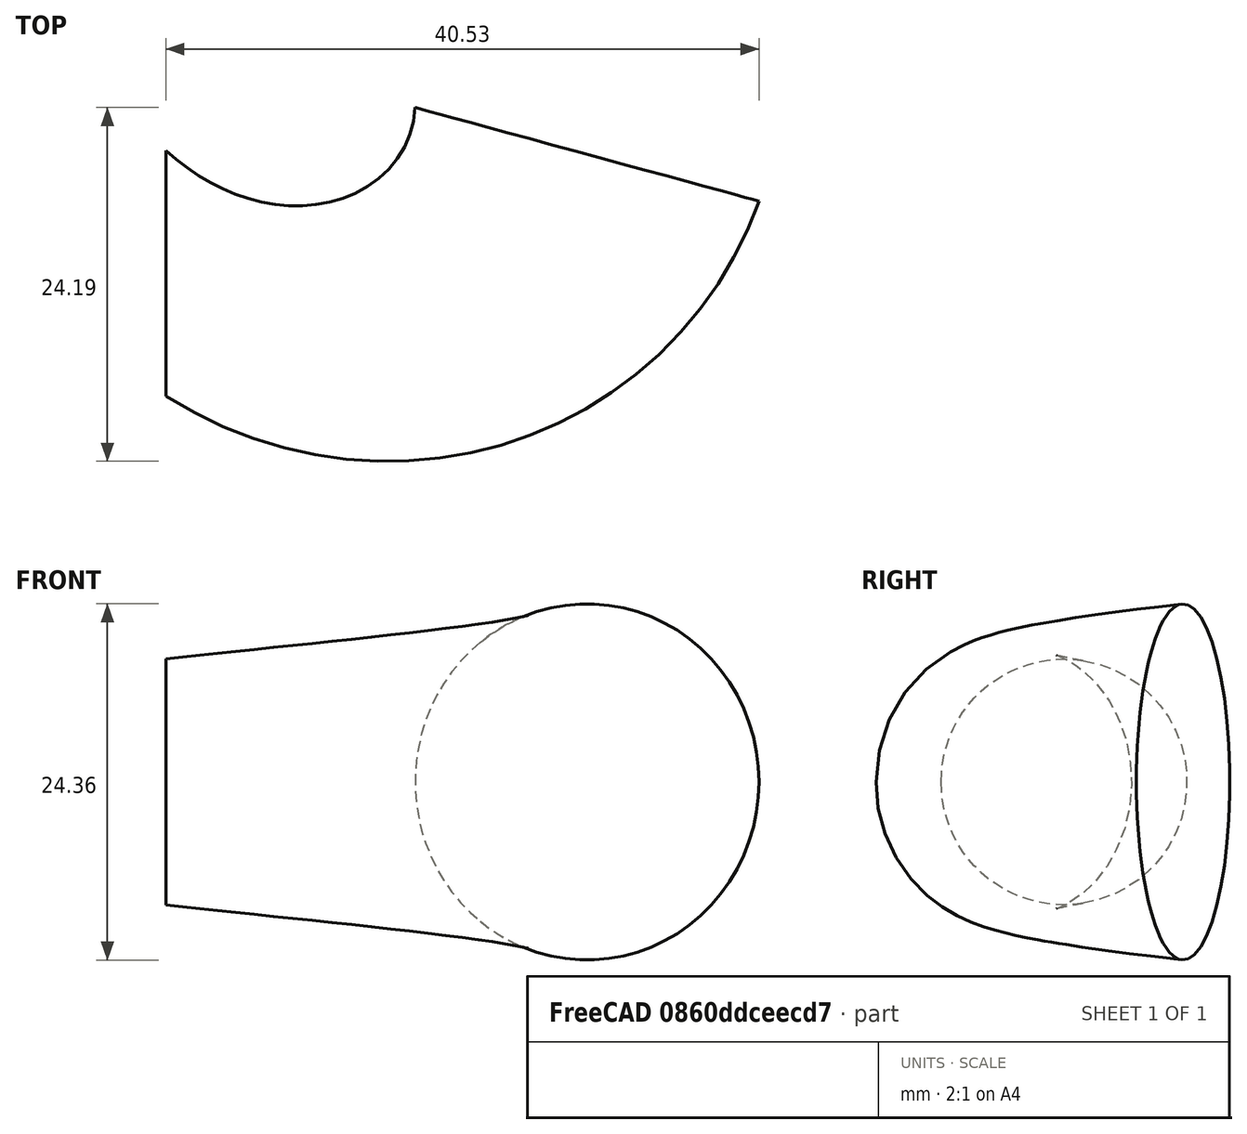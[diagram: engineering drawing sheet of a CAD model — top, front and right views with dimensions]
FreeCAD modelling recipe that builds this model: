
FCSTD DOCUMENT  (FreeCAD 1.0R39109 (Git))
Label: new-freecad
License: All rights reserved
LicenseURL: https://en.wikipedia.org/wiki/All_rights_reserved
objects: Part::Feature×25, Part::Part2DObjectPython×14, PartDesign::ShapeBinder×5, Sketcher::SketchObject×3, PartDesign::Plane×2, PartDesign::AdditivePipe×1, PartDesign::Body×1
note: 56 computed .brp shape members not serialized (recipe doc carries the construction recipe); baked Part::Feature solids carry a one-line shape summary decoded from their .brp

FEATURE [Sketcher::SketchObject] Sketch
  ArcFitTolerance = 1e-06
  AttachmentSupport = -> [XY_Plane]
  FullyConstrained = true
  MakeInternals = false
  MapMode = 5
FEATURE [Part::Feature] Line
  shape: bbox 24.24 x 2e-07 x 2e-07 mm, 0 faces, 0 solids (baked)
FEATURE [Part::Feature] Arc
  shape: bbox 16.41 x 12.57 x 2e-07 mm, 0 faces, 0 solids (baked)
FEATURE [Part::Feature] Arc001
  shape: bbox 16.41 x 12.57 x 2e-07 mm, 0 faces, 0 solids (baked)
FEATURE [Part::Feature] Line001
  shape: bbox 12.08 x 2e-07 x 2e-07 mm, 0 faces, 0 solids (baked)
FEATURE [Part::Feature] Arc002
  shape: bbox 4.831 x 3.711 x 2e-07 mm, 0 faces, 0 solids (baked)
FEATURE [Part::Feature] Arc003
  shape: bbox 4.872 x 50.24 x 2e-07 mm, 0 faces, 0 solids (baked)
FEATURE [Part::Feature] Arc004
  shape: bbox 11.42 x 106.4 x 2e-07 mm, 0 faces, 0 solids (baked)
FEATURE [Part::Feature] Line002
  shape: bbox 2e-07 x 15.35 x 2e-07 mm, 0 faces, 0 solids (baked)
FEATURE [Part::Feature] Line003
  shape: bbox 2.076 x 10.95 x 2e-07 mm, 0 faces, 0 solids (baked)
FEATURE [Part::Feature] Line004
  shape: bbox 5.231 x 2e-07 x 2e-07 mm, 0 faces, 0 solids (baked)
FEATURE [Part::Feature] Line005
  shape: bbox 13.57 x 4.192 x 2e-07 mm, 0 faces, 0 solids (baked)
FEATURE [Part::Feature] Line006
  shape: bbox 12.94 x 2.922 x 2e-07 mm, 0 faces, 0 solids (baked)
FEATURE [Part::Feature] Arc005
  shape: bbox 13.99 x 37.49 x 2e-07 mm, 0 faces, 0 solids (baked)
FEATURE [Part::Feature] Line007
  shape: bbox 3.445 x 16.84 x 2e-07 mm, 0 faces, 0 solids (baked)
FEATURE [Part::Feature] Line008
  shape: bbox 2e-07 x 0.8405 x 2e-07 mm, 0 faces, 0 solids (baked)
FEATURE [Part::Feature] Arc006
  shape: bbox 8 x 8 x 2e-07 mm, 0 faces, 0 solids (baked)
FEATURE [Part::Feature] Arc007
  shape: bbox 8 x 8 x 2e-07 mm, 0 faces, 0 solids (baked)
FEATURE [Part::Feature] Line009
  shape: bbox 2e-07 x 4.615 x 2e-07 mm, 0 faces, 0 solids (baked)
FEATURE [Part::Feature] Line010
  shape: bbox 2.883 x 9.356 x 2e-07 mm, 0 faces, 0 solids (baked)
FEATURE [Part::Feature] Arc008
  shape: bbox 0.2661 x 1.767 x 2e-07 mm, 0 faces, 0 solids (baked)
FEATURE [Part::Feature] Arc009
  shape: bbox 6.11 x 6.841 x 2e-07 mm, 0 faces, 0 solids (baked)
FEATURE [Part::Feature] Arc010
  shape: bbox 5.138 x 2.64 x 2e-07 mm, 0 faces, 0 solids (baked)
FEATURE [Part::Feature] Arc011
  shape: bbox 4 x 4 x 2e-07 mm, 0 faces, 0 solids (baked)
FEATURE [Part::Feature] Arc012
  shape: bbox 3.93 x 3.255 x 2e-07 mm, 0 faces, 0 solids (baked)
FEATURE [Part::Feature] Arc013
  shape: bbox 1.351 x 7.225 x 2e-07 mm, 0 faces, 0 solids (baked)
FEATURE [Part::Part2DObjectPython] Line012  # Draft 2D object (typed FeaturePython)
  Area = 0
  ChamferSize = 0
  Closed = false
  End = (330.971,-403.318,0)
  FilletRadius = 0
  Length = 20.7759
  MakeFace = true
  Placement = pos=(318.804,-386.478,0) rot=(0,0,1;0rad)
  Points = (2) [(0,0,0),(12.167,-16.8405,0)]
  Start = (318.804,-386.478,0)
  Subdivisions = 0
FEATURE [Part::Part2DObjectPython] Line013  # Draft 2D object (typed FeaturePython)
  Area = 0
  ChamferSize = 0
  Closed = false
  End = (347.383,-390.749,0)
  FilletRadius = 0
  Length = 25.0541
  MakeFace = true
  Placement = pos=(323.635,-382.766,0) rot=(0,0,1;0rad)
  Points = (2) [(0,0,0),(23.7484,-7.98259,0)]
  Start = (323.635,-382.766,0)
  Subdivisions = 0
FEATURE [Part::Part2DObjectPython] Line014  # Draft 2D object (typed FeaturePython)
  Area = 0
  ChamferSize = 0
  Closed = false
  End = (324.887,-394.898,0)
  FilletRadius = 0
  Length = 18.1608
  MakeFace = true
  Placement = pos=(306.727,-394.898,0) rot=(0,0,1;0rad)
  Points = (2) [(0,0,0),(18.1608,0,0)]
  Start = (306.727,-394.898,0)
  Subdivisions = 0
FEATURE [Part::Part2DObjectPython] Line015  # Draft 2D object (typed FeaturePython)
  Area = 0
  ChamferSize = 0
  Closed = false
  End = (318.782,-293.527,0)
  FilletRadius = 0
  Length = 25
  MakeFace = true
  Placement = pos=(342.094,-284.496,0) rot=(0,0,1;0rad)
  Points = (2) [(0,0,0),(-23.3117,-9.03134,0)]
  Start = (342.094,-284.496,0)
  Subdivisions = 0
FEATURE [Part::Part2DObjectPython] Line016  # Draft 2D object (typed FeaturePython)
  Area = 0
  ChamferSize = 0
  Closed = false
  End = (352.82,-330.261,0)
  FilletRadius = 0
  Length = 25
  MakeFace = true
  Placement = pos=(327.923,-332.529,0) rot=(0,0,1;0rad)
  Points = (2) [(0,0,0),(24.8969,2.26794,0)]
  Start = (327.923,-332.529,0)
  Subdivisions = 0
FEATURE [Part::Part2DObjectPython] Arc014  # Draft 2D object (typed FeaturePython)
  Area = 0
  FirstAngle = 0
  LastAngle = 36.4215
  MakeFace = false
  Placement = pos=(184.419,-345.592,0) rot=(0,0,-1;0.266003rad)
  Radius = 156.598
FEATURE [Part::Part2DObjectPython] Line017  # Draft 2D object (typed FeaturePython)
  Area = 0
  ChamferSize = 0
  Closed = false
  End = (341.307,-399.815,0)
  FilletRadius = 0
  Length = 24.1897
  MakeFace = true
  Placement = pos=(321.85,-385.443,0) rot=(0,0,1;0rad)
  Points = (2) [(0,0,0),(19.4572,-14.3721,0)]
  Start = (321.85,-385.443,0)
  Subdivisions = 0
FEATURE [Part::Part2DObjectPython] Arc015  # Draft 2D object (typed FeaturePython)
  Area = 0
  FirstAngle = 0
  LastAngle = 74.9303
  MakeFace = false
  Placement = pos=(324.887,-383.898,0) rot=(0,0,-1;1.5708rad)
  Radius = 11
FEATURE [Part::Part2DObjectPython] Line018  # Draft 2D object (typed FeaturePython)
  Area = 0
  ChamferSize = 0
  Closed = false
  End = (349.511,-309.008,0)
  FilletRadius = 0
  Length = 25
  MakeFace = true
  Placement = pos=(325.104,-314.417,0) rot=(0,0,1;0rad)
  Points = (2) [(0,0,0),(24.4079,5.40874,0)]
  Start = (325.104,-314.417,0)
  Subdivisions = 0
FEATURE [Part::Part2DObjectPython] Line019  # Draft 2D object (typed FeaturePython)
  Area = 0
  ChamferSize = 0
  Closed = false
  End = (327.923,-332.529,0)
  FilletRadius = 0
  Length = 18.3299
  MakeFace = true
  Placement = pos=(325.104,-314.417,0) rot=(0,0,1;0rad)
  Points = (2) [(0,0,0),(2.81996,-18.1117,0)]
  Start = (325.104,-314.417,0)
  Subdivisions = 0
FEATURE [Part::Part2DObjectPython] Line020  # Draft 2D object (typed FeaturePython)
  Area = 0
  ChamferSize = 0
  Closed = false
  End = (313.256,-327.03,0)
  FilletRadius = 0
  Length = 13.7263
  MakeFace = true
  Placement = pos=(326.514,-323.473,0) rot=(0,0,1;0rad)
  Points = (2) [(0,0,0),(-13.2574,-3.55713,0)]
  Start = (326.514,-323.473,0)
  Subdivisions = 0
FEATURE [Part::Part2DObjectPython] Arc016  # Draft 2D object (typed FeaturePython)
  Area = 0
  FirstAngle = 101.56
  LastAngle = 281.56
  MakeFace = true
  Placement = pos=(313.256,-327.03,0) rot=(0,0,1;0rad)
  Radius = 8.59532
FEATURE [Part::Part2DObjectPython] Line021  # Draft 2D object (typed FeaturePython)
  Area = 0
  ChamferSize = 0
  Closed = false
  End = (336.427,-266.58,0)
  FilletRadius = 0
  Length = 27.3519
  MakeFace = true
  Placement = pos=(311.109,-276.931,0) rot=(0,0,1;0rad)
  Points = (2) [(0,0,0),(25.318,10.3502,0)]
  Start = (311.109,-276.931,0)
  Subdivisions = 0
FEATURE [Part::Part2DObjectPython] Line022  # Draft 2D object (typed FeaturePython)
  Area = 0
  ChamferSize = 0
  Closed = false
  End = (330.438,-289.011,0)
  FilletRadius = 0
  Length = 18.5002
  MakeFace = true
  Placement = pos=(323.768,-271.755,0) rot=(0,0,1;0rad)
  Points = (2) [(0,0,0),(6.67012,-17.256,0)]
  Start = (323.768,-271.755,0)
  Subdivisions = 0
FEATURE [PartDesign::ShapeBinder] CopyLine014
  Placement = pos=(306.727,-394.898,0) rot=(0,0,1;0rad)
  TraceSupport = false
FEATURE [PartDesign::ShapeBinder] CopyLine015
  Placement = pos=(306.727,-394.898,0) rot=(0,0,1;0rad)
  TraceSupport = false
FEATURE [PartDesign::Plane] DatumPlane
  AttachmentSupport = -> [CopyLine014,CopyLine015]
  Length = 468.518
  MapMode = 7
  Placement = pos=(306.727,-394.898,0) rot=(0.57735,-0.57735,-0.57735;2.0944rad)
  ResizeMode = 0
  Width = 79.6274
FEATURE [Sketcher::SketchObject] Sketch001
  ArcFitTolerance = 1e-06
  AttachmentSupport = -> [DatumPlane]
  FullyConstrained = true
  MakeInternals = false
  MapMode = 5
  Placement = pos=(306.727,-394.898,0) rot=(0.57735,-0.57735,-0.57735;2.0944rad)
  sketch-geometry (1):
    g0: Circle CenterX=0 CenterY=0 CenterZ=0 NormalX=0 NormalY=0 NormalZ=1 AngleXU=0 Radius=8.4
  constraints (2):
    c: Coincident(g0,g-1)
    c: Diameter(g0) = 16.8
FEATURE [PartDesign::ShapeBinder] CopyArc014
  Placement = pos=(184.419,-345.592,0) rot=(0,0,-1;0.266003rad)
  TraceSupport = false
FEATURE [PartDesign::ShapeBinder] CopyArc015
  Placement = pos=(184.419,-345.592,0) rot=(0,0,-1;0.266003rad)
  TraceSupport = false
FEATURE [PartDesign::Plane] DatumPlane001
  AttachmentSupport = -> [CopyArc014,CopyArc015]
  Length = 517.988
  MapMode = 7
  Placement = pos=(335.509,-386.758,0) rot=(0.982567,-0.131459,-0.131459;1.58838rad)
  ResizeMode = 0
  Width = 81.2021
FEATURE [Sketcher::SketchObject] Sketch002
  ArcFitTolerance = 1e-06
  AttachmentSupport = -> [DatumPlane001]
  FullyConstrained = false
  MakeInternals = false
  MapMode = 5
  Placement = pos=(335.509,-386.758,0) rot=(0.982567,-0.131459,-0.131459;1.58838rad)
  sketch-geometry (1):
    g0: Circle CenterX=0 CenterY=0 CenterZ=0 NormalX=0 NormalY=0 NormalZ=1 AngleXU=0 Radius=12.177
  constraints (1):
    c: Coincident(g0,g-1)
FEATURE [PartDesign::ShapeBinder] CopyArc016
  Placement = pos=(324.887,-383.898,0) rot=(0,0,-1;1.5708rad)
  TraceSupport = false
FEATURE [PartDesign::AdditivePipe] AdditivePipe
  AuxilleryCurvelinear = true
  AuxillerySpineTangent = false
  Binormal = (0,0,0)
  Mode = 0
  Placement = pos=(335.509,-386.758,0) rot=(0.982567,-0.131459,-0.131459;1.58838rad)
  Profile = -> Sketch002
  Refine = true
  Sections = -> [Sketch001]
  Spine = -> CopyArc016 [Edge1]
  SpineTangent = false
  Suppressed = false
  Transformation = 1
  Transition = 0
FEATURE [PartDesign::Body] Body
  AllowCompound = false
  Group = -> [Sketch,DatumPlane,CopyLine014,CopyLine015,Sketch001,DatumPlane001,CopyArc014,CopyArc015,Sketch002,AdditivePipe,CopyArc016]
  Origin = -> Origin
  Tip = -> AdditivePipe
